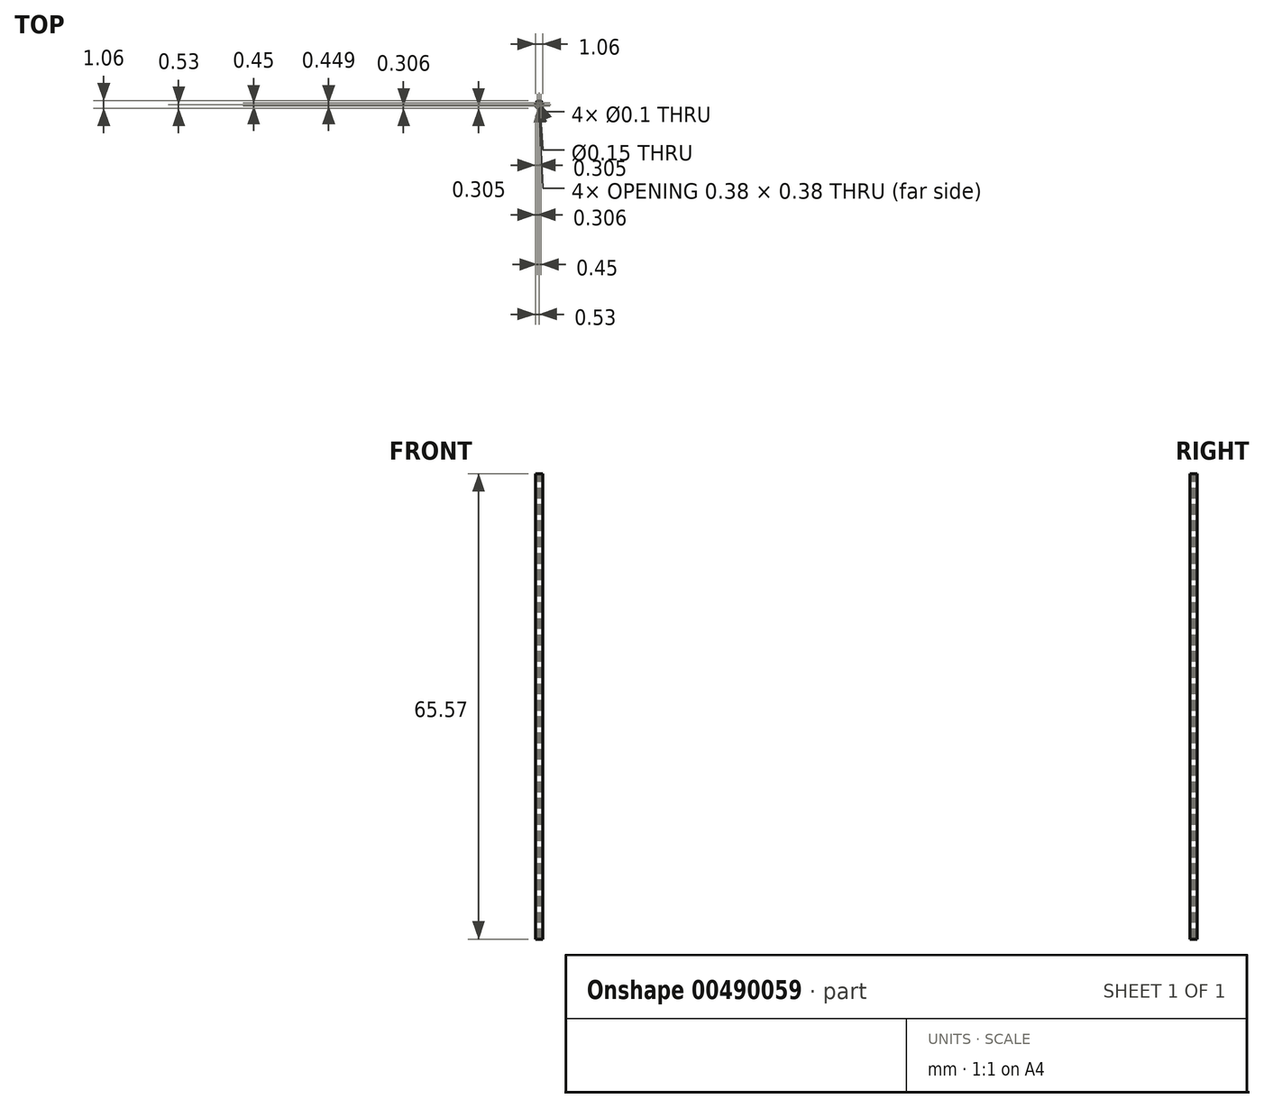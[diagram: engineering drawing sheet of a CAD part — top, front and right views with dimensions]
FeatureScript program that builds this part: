
annotation { "Feature Type Name" : "Feature", "Feature Type Description" : "" }
export const myFeature = defineFeature(function(context is Context, id is Id, definition is map)
    precondition{}
    {
        {
            var Q0;
            Q0=qCreatedBy(makeId("Top.planeOp"),FACE);
            var sketch = newSketch(context, id + "F0", { "sketchPlane" : qUnion([Q0])});
            skCircle(sketch, "E0", {"center": v(0, 0) * mm, "radius": 0.52 * mm});
            skCircle(sketch, "E1", {"center": v(0, 0) * mm, "radius": 0.07 * mm});
            skCircle(sketch, "E2", {"center": v(0, 0) * mm, "radius": 0.23 * mm, "construction": true});
            skCircle(sketch, "E3", {"center": v(-0.23, 0) * mm, "radius": 0.05 * mm});
            skArc(sketch, "E4", {"start": v(-0.08, -0.37) * mm, "mid": v(-0.27, -0.27) * mm, "end": v(-0.37, -0.08) * mm, "construction": true});
            skLineSegment(sketch, "E5", {"start": v(0, 0) * mm, "end": v(-0.51, -0.12) * mm, "construction": true});
            skLineSegment(sketch, "E6", {"start": v(0, 0) * mm, "end": v(-0.12, -0.51) * mm, "construction": true});
            skArc(sketch, "E7.0.startCap", {"start": v(-0.07, -0.32) * mm, "mid": v(-0.03, -0.38) * mm, "end": v(-0.1, -0.41) * mm});
            skArc(sketch, "E7.0.endCap", {"start": v(-0.41, -0.1) * mm, "mid": v(-0.38, -0.03) * mm, "end": v(-0.32, -0.07) * mm});
            skArc(sketch, "E7.0.left", {"start": v(-0.1, -0.41) * mm, "mid": v(-0.3, -0.3) * mm, "end": v(-0.41, -0.1) * mm});
            skArc(sketch, "E7.0.right", {"start": v(-0.07, -0.32) * mm, "mid": v(-0.23, -0.23) * mm, "end": v(-0.32, -0.07) * mm});
            skCircle(sketch, "E8.1.0", {"center": v(0, -0.23) * mm, "radius": 0.05 * mm});
            skCircle(sketch, "E8.2.0", {"center": v(0.22, 0) * mm, "radius": 0.05 * mm});
            skCircle(sketch, "E8.3.0", {"center": v(0, 0.22) * mm, "radius": 0.05 * mm});
            skArc(sketch, "E9.1.0", {"start": v(0.32, -0.07) * mm, "mid": v(0.23, -0.23) * mm, "end": v(0.07, -0.32) * mm});
            skArc(sketch, "E9.1.1", {"start": v(0.1, -0.41) * mm, "mid": v(0.03, -0.38) * mm, "end": v(0.07, -0.32) * mm});
            skArc(sketch, "E9.1.2", {"start": v(0.41, -0.1) * mm, "mid": v(0.3, -0.3) * mm, "end": v(0.1, -0.41) * mm});
            skArc(sketch, "E9.1.3", {"start": v(0.32, -0.07) * mm, "mid": v(0.38, -0.03) * mm, "end": v(0.41, -0.1) * mm});
            skArc(sketch, "E9.2.0", {"start": v(0.07, 0.32) * mm, "mid": v(0.23, 0.23) * mm, "end": v(0.32, 0.07) * mm});
            skArc(sketch, "E9.2.1", {"start": v(0.41, 0.1) * mm, "mid": v(0.38, 0.03) * mm, "end": v(0.32, 0.07) * mm});
            skArc(sketch, "E9.2.2", {"start": v(0.1, 0.41) * mm, "mid": v(0.3, 0.3) * mm, "end": v(0.41, 0.1) * mm});
            skArc(sketch, "E9.2.3", {"start": v(0.07, 0.32) * mm, "mid": v(0.03, 0.38) * mm, "end": v(0.1, 0.41) * mm});
            skArc(sketch, "E9.3.0", {"start": v(-0.32, 0.07) * mm, "mid": v(-0.23, 0.23) * mm, "end": v(-0.07, 0.32) * mm});
            skArc(sketch, "E9.3.1", {"start": v(-0.1, 0.41) * mm, "mid": v(-0.03, 0.38) * mm, "end": v(-0.07, 0.32) * mm});
            skArc(sketch, "E9.3.2", {"start": v(-0.41, 0.1) * mm, "mid": v(-0.3, 0.3) * mm, "end": v(-0.1, 0.41) * mm});
            skArc(sketch, "E9.3.3", {"start": v(-0.32, 0.07) * mm, "mid": v(-0.38, 0.03) * mm, "end": v(-0.41, 0.1) * mm});
            skSolve(sketch);
        }
        {
            var Q0;
            Q0=qCreatedBy(makeId("Right.planeOp"),FACE);
            var sketch = newSketch(context, id + "F1", { "sketchPlane" : qUnion([Q0])});
            skFitSpline(sketch, "E10", {"points": [v(0, 0) * mm, v(0, 65.57) * mm], "startDerivative": vector(0, 103.62) * mm, "endDerivative": vector(0, 42.74) * mm});
            skSolve(sketch);
        }
        {
            var Q0;
            Q0=makeQuery(id+"F0.imprint","IMPRINT",FACE,{"disambiguationData":[TD([[makeQuery(id+"F0.imprint","IMPRINT",EDGE,{"derivedFrom":sQuery(id+"F0.wireOp",EDGE,"E0")}),1.0]])]});
            var Q1;
            Q1=sQuery(id+"F1.wireOp",EDGE,"E10");
            sweep(context, id + "F2", {"profiles" : qUnion([Q0]), "path" : qUnion([Q1])});
        }
    });
